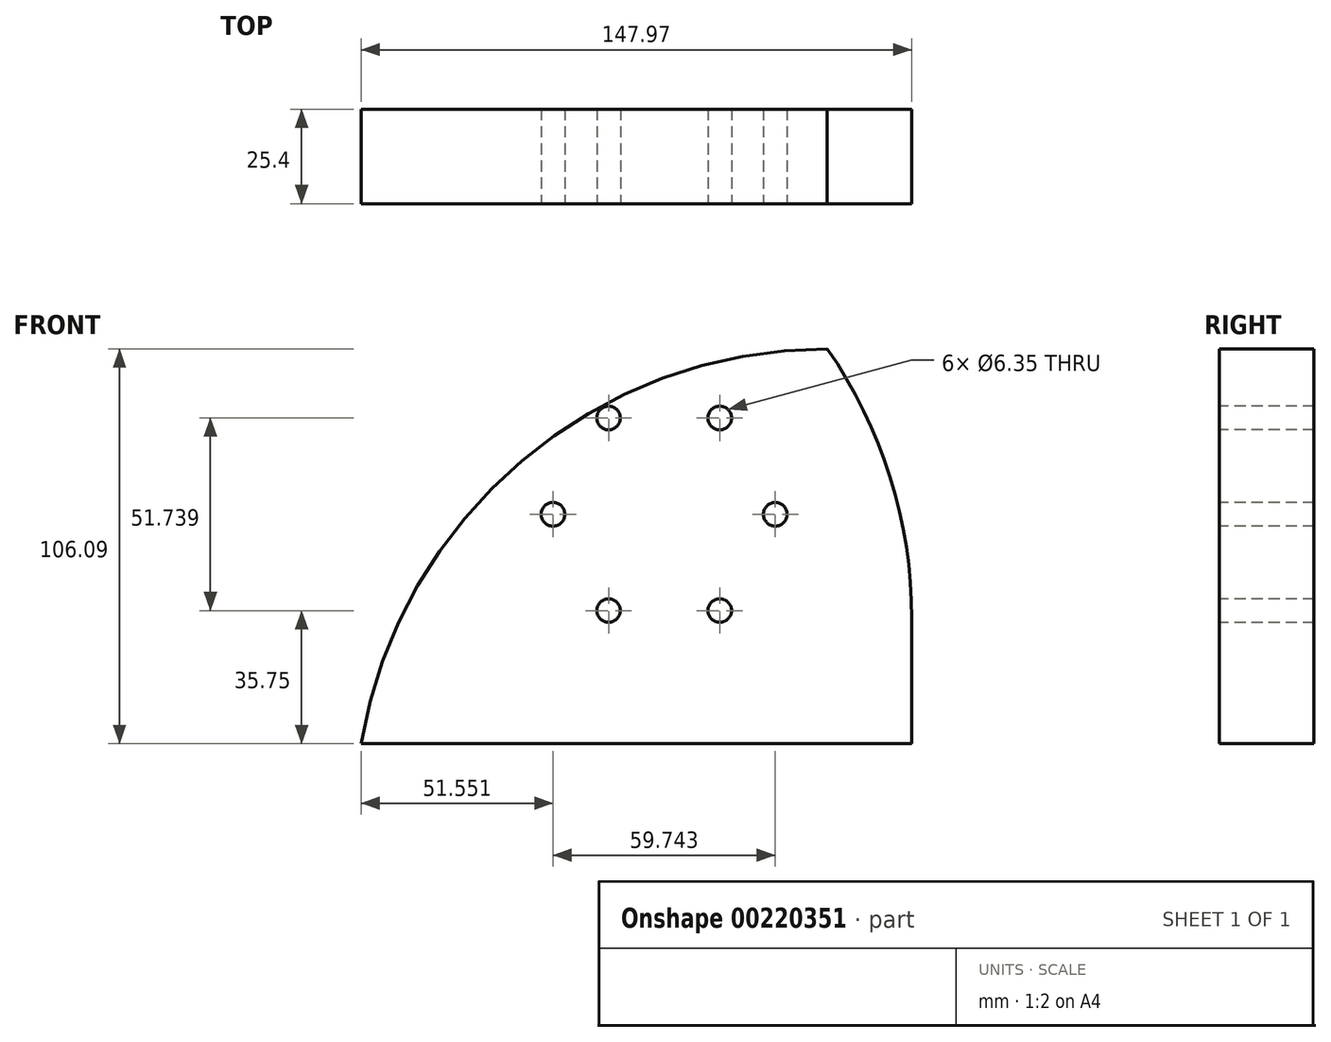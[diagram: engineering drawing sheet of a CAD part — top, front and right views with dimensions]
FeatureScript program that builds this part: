
annotation { "Feature Type Name" : "Feature", "Feature Type Description" : "" }
export const myFeature = defineFeature(function(context is Context, id is Id, definition is map)
    precondition{}
    {
        {
            var Q0;
            Q0=qCreatedBy(makeId("Front.planeOp"),FACE);
            var sketch = newSketch(context, id + "F0", { "sketchPlane" : qUnion([Q0])});
            skLineSegment(sketch, "E0.bottom", {"start": v(-74.1, 44.47) * mm, "end": v(73.88, 44.47) * mm});
            skLineSegment(sketch, "E0.top", {"start": v(-74.1, -61.62) * mm, "end": v(73.88, -61.62) * mm});
            skLineSegment(sketch, "E0.left", {"start": v(-74.1, 44.47) * mm, "end": v(-74.1, -61.62) * mm});
            skLineSegment(sketch, "E0.right", {"start": v(73.88, 44.47) * mm, "end": v(73.88, -61.62) * mm});
            skSolve(sketch);
        }
        {
            var Q0;
            Q0 = qSketchRegion(id + "F0", true);
            extrude(context, id + "F1", {"entities" : qUnion([Q0]), "endBound" : BoundingType.SYMMETRIC, "depth" : 25.4 * mm});
        }
        {
            var Q0;
            Q0=makeQuery(id+"F1.opExtrude","SWEPT_EDGE",EDGE,{"disambiguationData":[OSD([sQuery(id+"F0.wireOp",EDGE,"E0.bottom"),sQuery(id+"F0.wireOp",EDGE,"E0.left")])]});
            fillet(context, id + "F2", {"entities" : qUnion([Q0]), "radius" : 127 * mm, "tangentPropagation" : true, "allowEdgeOverflow" : false});
        }
        {
            var Q0;
            Q0=makeQuery(id+"F1.opExtrude","SWEPT_EDGE",EDGE,{"disambiguationData":[OSD([sQuery(id+"F0.wireOp",EDGE,"E0.bottom"),sQuery(id+"F0.wireOp",EDGE,"E0.right")])]});
            fillet(context, id + "F3", {"entities" : qUnion([Q0]), "radius" : 127 * mm, "tangentPropagation" : true, "allowEdgeOverflow" : false});
        }
        {
            var Q0;
            Q0=makeQuery(id+"F1.opExtrude","CAP_FACE",FACE,{"disambiguationData":[OSD([sQuery(id+"F0.wireOp",EDGE,"E0.bottom"),sQuery(id+"F0.wireOp",EDGE,"E0.top"),sQuery(id+"F0.wireOp",EDGE,"E0.left"),sQuery(id+"F0.wireOp",EDGE,"E0.right")])],"isStart":false});
            var sketch = newSketch(context, id + "F4", { "sketchPlane" : qUnion([Q0])});
            skCircle(sketch, "E1.cCircle", {"center": v(7.33, 0) * mm, "radius": 25.87 * mm, "construction": true});
            skLineSegment(sketch, "E1.0", {"start": v(-7.6, 25.87) * mm, "end": v(22.27, 25.87) * mm});
            skLineSegment(sketch, "E1.1", {"start": v(22.27, 25.87) * mm, "end": v(37.2, 0) * mm});
            skLineSegment(sketch, "E1.2", {"start": v(37.2, 0) * mm, "end": v(22.27, -25.87) * mm});
            skLineSegment(sketch, "E1.3", {"start": v(22.27, -25.87) * mm, "end": v(-7.6, -25.87) * mm});
            skLineSegment(sketch, "E1.4", {"start": v(-7.6, -25.87) * mm, "end": v(-22.54, 0) * mm});
            skLineSegment(sketch, "E1.5", {"start": v(-22.54, 0) * mm, "end": v(-7.6, 25.87) * mm});
            skPoint(sketch, "E1.0.midPoint", {"position": v(7.33, 25.87) * mm});
            skSolve(sketch);
        }
        {
            var Q0;
            Q0=sQuery(id+"F4.wireOp",VERTEX,"E1.4.start");
            var Q1;
            Q1=sQuery(id+"F4.wireOp",VERTEX,"E1.5.start");
            var Q2;
            Q2=sQuery(id+"F4.wireOp",VERTEX,"E1.5.end");
            var Q3;
            Q3=sQuery(id+"F4.wireOp",VERTEX,"E1.0.end");
            var Q4;
            Q4=sQuery(id+"F4.wireOp",VERTEX,"E1.2.start");
            var Q5;
            Q5=sQuery(id+"F4.wireOp",VERTEX,"E1.2.end");
            var Q6;
            Q6=makeQuery(id+"F1.opExtrude","SWEPT_BODY",BODY,{"disambiguationData":[OSD([sQuery(id+"F0.wireOp",EDGE,"E0.bottom"),sQuery(id+"F0.wireOp",EDGE,"E0.top"),sQuery(id+"F0.wireOp",EDGE,"E0.left"),sQuery(id+"F0.wireOp",EDGE,"E0.right")])]});
            hole(context, id + "F5", {"style" : HoleStyle.SIMPLE, "endStyle" : HoleEndStyle.THROUGH, "holeDiameter" : 6.35 * mm, "locations" : qUnion([Q0, Q1, Q2, Q3, Q4, Q5]), "scope" : qUnion([Q6]), "isTappedThrough" : true});
        }
    });
